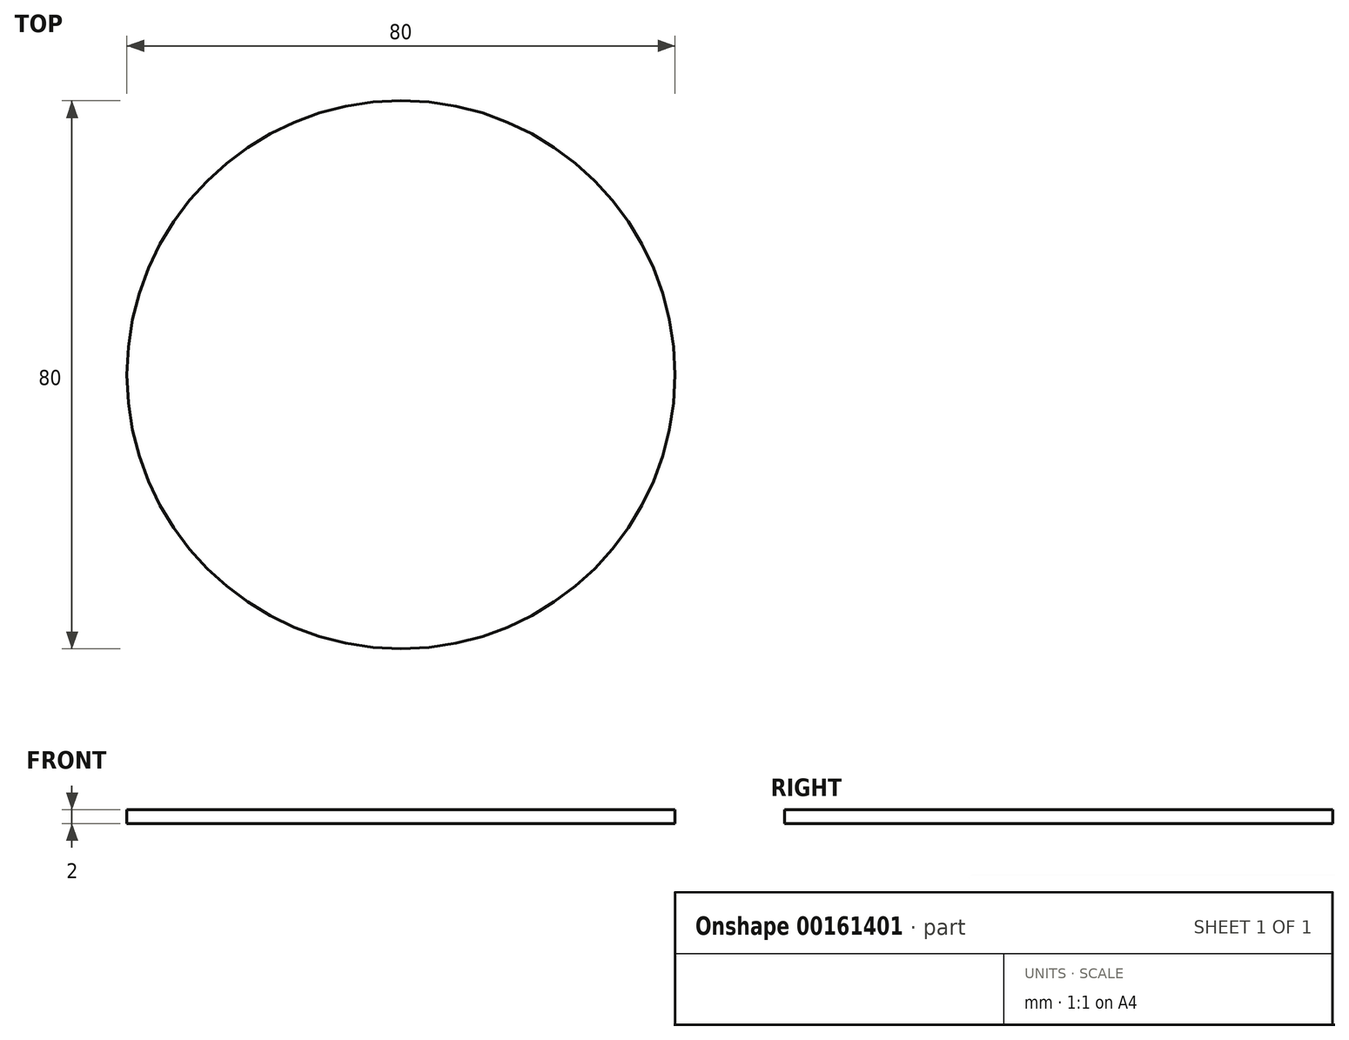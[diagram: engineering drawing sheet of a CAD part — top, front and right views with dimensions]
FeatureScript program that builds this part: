
annotation { "Feature Type Name" : "Feature", "Feature Type Description" : "" }
export const myFeature = defineFeature(function(context is Context, id is Id, definition is map)
    precondition{}
    {
        {
            var Q0;
            Q0=qCreatedBy(makeId("Top.planeOp"),FACE);
            var sketch = newSketch(context, id + "F1", { "sketchPlane" : qUnion([Q0])});
            skCircle(sketch, "E0", {"center": v(0, 0) * mm, "radius": 40 * mm});
            skSolve(sketch);
        }
        {
            var Q0;
            Q0=makeQuery(id+"F1.imprint","IMPRINT",FACE,{"disambiguationData":[TD([[makeQuery(id+"F1.imprint","IMPRINT",EDGE,{"derivedFrom":sQuery(id+"F1.wireOp",EDGE,"E0")}),1.0]])]});
            extrude(context, id + "F0", {"entities" : qUnion([Q0]), "depth" : 2 * mm});
        }
    });
